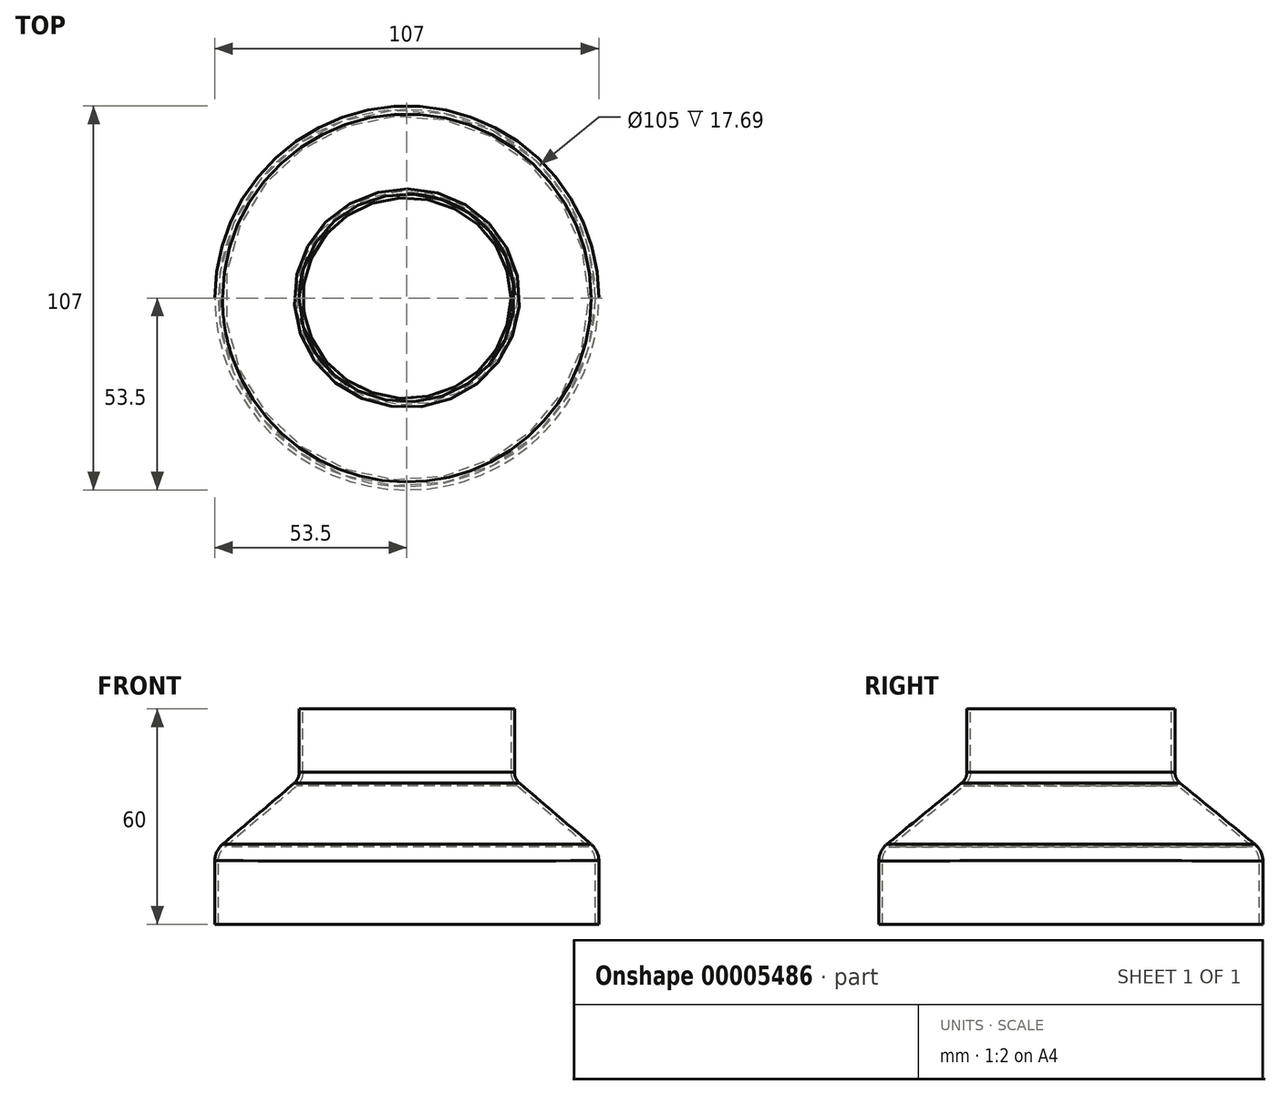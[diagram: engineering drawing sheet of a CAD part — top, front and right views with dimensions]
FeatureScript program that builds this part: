
annotation { "Feature Type Name" : "Feature", "Feature Type Description" : "" }
export const myFeature = defineFeature(function(context is Context, id is Id, definition is map)
    precondition{}
    {
        {
            var Q0;
            Q0=qCreatedBy(makeId("Top.planeOp"),FACE);
            var sketch = newSketch(context, id + "F0", { "sketchPlane" : qUnion([Q0])});
            skCircle(sketch, "E0", {"center": v(0, 0) * mm, "radius": 52.5 * mm});
            skSolve(sketch);
        }
        {
            var Q0;
            Q0=qCreatedBy(makeId("Top.planeOp"),FACE);
            cPlane(context, id + "F1", {"entities" : qUnion([Q0]), "cplaneType" : CPlaneType.OFFSET, "offset" : 20 * mm, "width" : 150 * mm, "height" : 150 * mm});
        }
        {
            var Q0;
            Q0=qCreatedBy(id+"F1.planeOp",FACE);
            var sketch = newSketch(context, id + "F2", { "sketchPlane" : qUnion([Q0])});
            skPoint(sketch, "E1.0", {"position": v(0, 0) * mm});
            skEllipse(sketch, "E2", {"center": v(0, 0) * mm, "majorRadius": 29 * mm, "minorRadius": 28 * mm, "majorAxis": v(1, 0)});
            skSolve(sketch);
        }
        {
            var Q0;
            Q0=makeQuery(id+"F2.imprint","IMPRINT",FACE,{"disambiguationData":[TD([[makeQuery(id+"F2.imprint","IMPRINT",EDGE,{"derivedFrom":sQuery(id+"F2.wireOp",EDGE,"E2")}),1.0]])]});
            var Q1;
            Q1=sQuery(id+"F2.wireOp",EDGE,"E2");
            extrude(context, id + "F3", {"entities" : qUnion([Q0]), "surfaceEntities" : qUnion([Q1]), "depth" : 20 * mm});
        }
        {
            var Q1;
            Q1=makeQuery(id+"F0.imprint","IMPRINT",FACE,{"disambiguationData":[TD([[makeQuery(id+"F0.imprint","IMPRINT",EDGE,{"derivedFrom":sQuery(id+"F0.wireOp",EDGE,"E0")}),1.0]])]});
            var Q2;
            Q2=makeQuery(id+"F3.opExtrude","CAP_FACE",FACE,{"disambiguationData":[OSD([sQuery(id+"F2.wireOp",EDGE,"E2")])],"isStart":true});
            var Q3;
            Q3=sQuery(id+"F0.wireOp",EDGE,"E0");
            var Q4;
            Q4=makeQuery(id+"F3.opExtrude","CAP_EDGE",EDGE,{"disambiguationData":[OSD([sQuery(id+"F2.wireOp",EDGE,"E2")])],"isStart":true});
            loft(context, id + "F4", {"operationType" : NewBodyOperationType.ADD, "sheetProfilesArray" : [{ "sheetProfileEntities" : qUnion([Q1]) }, { "sheetProfileEntities" : qUnion([Q2]) }], "wireProfilesArray" : [{ "wireProfileEntities" : qUnion([Q3]) }, { "wireProfileEntities" : qUnion([Q4]) }]});
        }
        {
            var Q0;
            Q0=makeQuery(id+"F0.imprint","IMPRINT",FACE,{"disambiguationData":[TD([[makeQuery(id+"F0.imprint","IMPRINT",EDGE,{"derivedFrom":sQuery(id+"F0.wireOp",EDGE,"E0")}),1.0]])]});
            var Q1;
            Q1=sQuery(id+"F0.wireOp",EDGE,"E0");
            extrude(context, id + "F5", {"entities" : qUnion([Q0]), "operationType" : NewBodyOperationType.ADD, "surfaceEntities" : qUnion([Q1]), "oppositeDirection" : true, "depth" : 20 * mm});
        }
        {
            var Q0;
            {var subQ0=sQuery(id+"F2.wireOp",EDGE,"E2");Q0=makeQuery(id+"F4.boolean.opBoolean","MERGE",EDGE,{"derivedFrom":[makeQuery(id+"F3.opExtrude","CAP_EDGE",EDGE,{"disambiguationData":[OSD([subQ0])],"isStart":true}),makeQuery(id+"F4.opLoft","MID_CAP_EDGE",EDGE,{"disambiguationData":[OSD([sQuery(id+"F0.wireOp",EDGE,"E0"),subQ0])],"capPos":1.0})]});}
            var Q1;
            {var subQ0=sQuery(id+"F0.wireOp",EDGE,"E0");Q1=makeQuery(id+"F5.boolean.opBoolean","MERGE",EDGE,{"derivedFrom":[makeQuery(id+"F4.opLoft","MID_CAP_EDGE",EDGE,{"disambiguationData":[OSD([subQ0])],"capPos":0.0}),makeQuery(id+"F5.opExtrude","CAP_EDGE",EDGE,{"disambiguationData":[OSD([subQ0])],"isStart":true})]});}
            fillet(context, id + "F6", {"entities" : qUnion([Q0, Q1]), "radius" : 5 * mm, "tangentPropagation" : true, "allowEdgeOverflow" : false});
        }
        {
            var Q0;
            Q0=makeQuery(id+"F3.opExtrude","CAP_FACE",FACE,{"disambiguationData":[OSD([sQuery(id+"F2.wireOp",EDGE,"E2")])],"isStart":false});
            var Q1;
            Q1=makeQuery(id+"F5.opExtrude","CAP_FACE",FACE,{"disambiguationData":[OSD([sQuery(id+"F0.wireOp",EDGE,"E0")])],"isStart":false});
            shell(context, id + "F7", {"entities" : qUnion([Q0, Q1]), "thickness" : 1 * mm, "oppositeDirection" : true});
        }
    });
